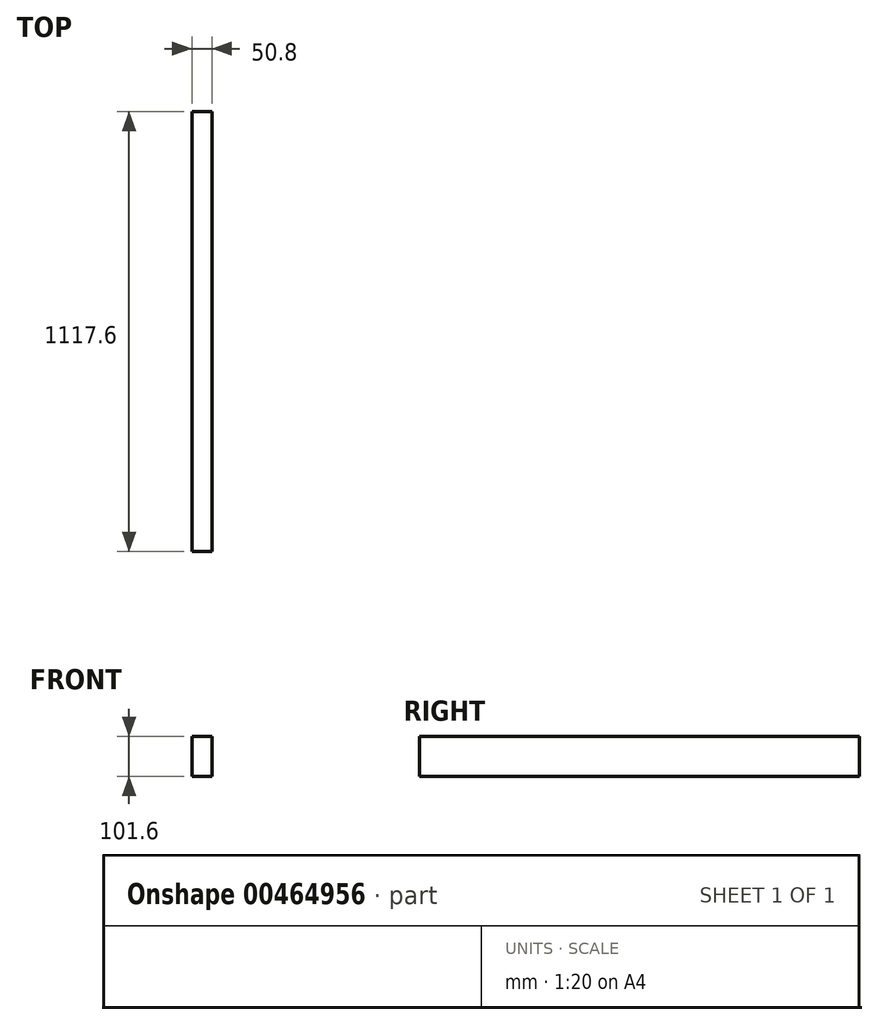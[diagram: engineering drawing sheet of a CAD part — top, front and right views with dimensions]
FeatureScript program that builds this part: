
annotation { "Feature Type Name" : "Feature", "Feature Type Description" : "" }
export const myFeature = defineFeature(function(context is Context, id is Id, definition is map)
    precondition{}
    {
        {
            var Q0;
            Q0=qCreatedBy(makeId("Top.planeOp"),FACE);
            var sketch = newSketch(context, id + "F0", { "sketchPlane" : qUnion([Q0])});
            skLineSegment(sketch, "E0.bottom", {"start": v(-25.4, 558.8) * mm, "end": v(25.4, 558.8) * mm});
            skLineSegment(sketch, "E0.top", {"start": v(-25.4, -558.8) * mm, "end": v(25.4, -558.8) * mm});
            skLineSegment(sketch, "E0.left", {"start": v(-25.4, 558.8) * mm, "end": v(-25.4, -558.8) * mm});
            skLineSegment(sketch, "E0.right", {"start": v(25.4, 558.8) * mm, "end": v(25.4, -558.8) * mm});
            skPoint(sketch, "E0.middle", {"position": v(0, 0) * mm});
            skSolve(sketch);
        }
        {
            var Q0;
            Q0=makeQuery(id+"F0.imprint","IMPRINT",FACE,{"disambiguationData":[TD([[makeQuery(id+"F0.imprint","IMPRINT",EDGE,{"derivedFrom":sQuery(id+"F0.wireOp",EDGE,"E0.bottom")}),-1.0]])]});
            extrude(context, id + "F1", {"entities" : qUnion([Q0]), "depth" : 101.6 * mm});
        }
    });
